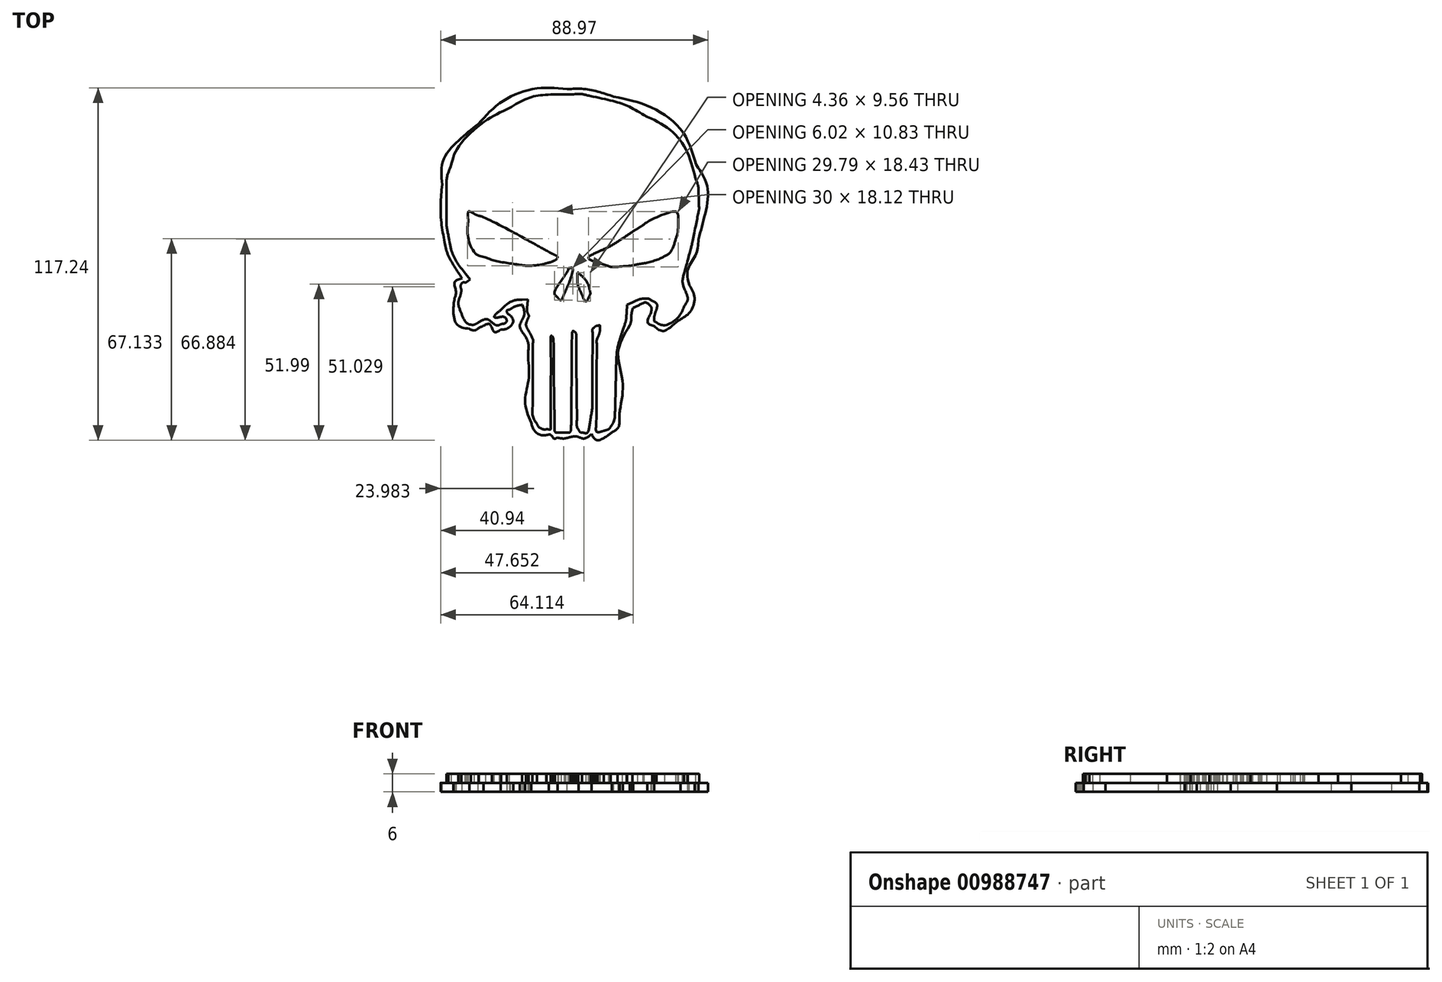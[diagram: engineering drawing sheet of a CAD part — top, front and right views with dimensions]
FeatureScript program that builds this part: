
annotation { "Feature Type Name" : "Feature", "Feature Type Description" : "" }
export const myFeature = defineFeature(function(context is Context, id is Id, definition is map)
    precondition{}
    {
        {
            var Q0;
            Q0=qCreatedBy(makeId("Top.planeOp"),FACE);
            var sketch = newSketch(context, id + "F0", { "sketchPlane" : qUnion([Q0])});
            skLineSegment(sketch, "E0", {"start": v(-15.1, -13.85) * mm, "end": v(-14.93, -11.9) * mm});
            skLineSegment(sketch, "E1", {"start": v(-14.93, -11.9) * mm, "end": v(-16.83, -12.05) * mm});
            skLineSegment(sketch, "E2", {"start": v(-34.82, -5.82) * mm, "end": v(-34.16, -5.31) * mm});
            skLineSegment(sketch, "E3", {"start": v(-34.16, -5.31) * mm, "end": v(-35.58, -3.44) * mm});
            skLineSegment(sketch, "E4", {"start": v(19.8, -12.99) * mm, "end": v(18.07, -13.76) * mm});
            skLineSegment(sketch, "E5", {"start": v(18.07, -13.76) * mm, "end": v(17.92, -16.33) * mm});
            skFitSpline(sketch, "E6", {"points": [v(-5.85, -56) * mm, v(-5.95, -55.85) * mm, v(-6.1, -50.74) * mm, v(-6.17, -44.65) * mm]});
            skFitSpline(sketch, "E7", {"points": [v(-6.17, -44.65) * mm, v(-6.3, -32.8) * mm, v(-6.66, -24.47) * mm, v(-7.03, -24.1) * mm]});
            skFitSpline(sketch, "E8", {"points": [v(-7.03, -24.1) * mm, v(-7.16, -23.97) * mm, v(-7.26, -30.62) * mm, v(-7.27, -38.88) * mm]});
            skFitSpline(sketch, "E9", {"points": [v(-7.27, -38.88) * mm, v(-7.27, -55.07) * mm, v(-7.28, -55.17) * mm, v(-8.71, -55.17) * mm]});
            skFitSpline(sketch, "E10", {"points": [v(-8.71, -55.17) * mm, v(-9.86, -55.17) * mm, v(-11.3, -54.34) * mm, v(-11.92, -53.32) * mm]});
            skFitSpline(sketch, "E11", {"points": [v(-11.92, -53.32) * mm, v(-13.14, -51.36) * mm, v(-13.36, -48.77) * mm, v(-13.28, -37.24) * mm]});
            skFitSpline(sketch, "E12", {"points": [v(-13.28, -37.24) * mm, v(-13.2, -25.74) * mm, v(-13.26, -25.16) * mm, v(-14.73, -22.3) * mm]});
            skFitSpline(sketch, "E13", {"points": [v(-14.73, -22.3) * mm, v(-15.4, -21) * mm, v(-15.46, -19.77) * mm, v(-14.92, -18.44) * mm]});
            skFitSpline(sketch, "E14", {"points": [v(-14.92, -18.44) * mm, v(-14.6, -17.66) * mm, v(-14.6, -17.34) * mm, v(-14.9, -16.64) * mm]});
            skFitSpline(sketch, "E15", {"points": [v(-14.9, -16.64) * mm, v(-15.13, -16.08) * mm, v(-15.2, -15.14) * mm, v(-15.1, -13.85) * mm]});
            skFitSpline(sketch, "E16", {"points": [v(-16.83, -12.05) * mm, v(-19.3, -12.25) * mm, v(-21.71, -13.44) * mm, v(-24.06, -15.6) * mm]});
            skFitSpline(sketch, "E17", {"points": [v(-24.06, -15.6) * mm, v(-25.97, -17.35) * mm, v(-26.08, -17.91) * mm, v(-24.52, -17.91) * mm]});
            skFitSpline(sketch, "E18", {"points": [v(-24.52, -17.91) * mm, v(-22.55, -17.91) * mm, v(-22.04, -19.45) * mm, v(-23.78, -20.17) * mm]});
            skFitSpline(sketch, "E19", {"points": [v(-23.78, -20.17) * mm, v(-24.74, -20.57) * mm, v(-25.8, -20.37) * mm, v(-26.93, -19.57) * mm]});
            skFitSpline(sketch, "E20", {"points": [v(-26.93, -19.57) * mm, v(-28.3, -18.59) * mm, v(-29.38, -18.6) * mm, v(-31.32, -19.61) * mm]});
            skFitSpline(sketch, "E21", {"points": [v(-31.32, -19.61) * mm, v(-32.62, -20.3) * mm, v(-33.25, -20.47) * mm, v(-33.82, -20.33) * mm]});
            skFitSpline(sketch, "E22", {"points": [v(-33.82, -20.33) * mm, v(-34.92, -20.05) * mm, v(-36.3, -18.42) * mm, v(-37.02, -16.56) * mm]});
            skFitSpline(sketch, "E23", {"points": [v(-37.02, -16.56) * mm, v(-37.91, -14.22) * mm, v(-38.02, -12.89) * mm, v(-37.47, -10.98) * mm]});
            skFitSpline(sketch, "E24", {"points": [v(-37.47, -10.98) * mm, v(-37.2, -10.06) * mm, v(-37.05, -8.9) * mm, v(-37.14, -8.38) * mm]});
            skFitSpline(sketch, "E25", {"points": [v(-37.14, -8.38) * mm, v(-37.3, -7.41) * mm, v(-36.62, -6.35) * mm, v(-35.84, -6.33) * mm]});
            skFitSpline(sketch, "E26", {"points": [v(-35.84, -6.33) * mm, v(-35.64, -6.33) * mm, v(-35.19, -6.1) * mm, v(-34.82, -5.82) * mm]});
            skFitSpline(sketch, "E27", {"points": [v(-35.58, -3.44) * mm, v(-38.7, 0.67) * mm, v(-40.31, 4.22) * mm, v(-41.31, 9.1) * mm]});
            skFitSpline(sketch, "E28", {"points": [v(-41.31, 9.1) * mm, v(-41.85, 11.75) * mm, v(-41.94, 13.08) * mm, v(-41.96, 19.34) * mm]});
            skFitSpline(sketch, "E29", {"points": [v(-41.96, 19.34) * mm, v(-41.98, 26.96) * mm, v(-41.71, 29.24) * mm, v(-40.4, 32.73) * mm]});
            skFitSpline(sketch, "E30", {"points": [v(-40.4, 32.73) * mm, v(-38.28, 38.4) * mm, v(-29.23, 47.3) * mm, v(-21.14, 51.66) * mm]});
            skFitSpline(sketch, "E31", {"points": [v(-21.14, 51.66) * mm, v(-15.26, 54.83) * mm, v(-10.37, 56.02) * mm, v(-2.4, 56.23) * mm]});
            skFitSpline(sketch, "E32", {"points": [v(-2.4, 56.23) * mm, v(2.5, 56.37) * mm, v(3.29, 56.32) * mm, v(5.78, 55.75) * mm]});
            skFitSpline(sketch, "E33", {"points": [v(5.78, 55.75) * mm, v(14.08, 53.86) * mm, v(18.54, 52.28) * mm, v(23.7, 49.37) * mm]});
            skFitSpline(sketch, "E34", {"points": [v(23.7, 49.37) * mm, v(32.2, 44.6) * mm, v(37.67, 37.9) * mm, v(40.88, 28.37) * mm]});
            skFitSpline(sketch, "E35", {"points": [v(40.88, 28.37) * mm, v(41.66, 26.03) * mm, v(41.8, 25.2) * mm, v(41.9, 21.88) * mm]});
            skFitSpline(sketch, "E36", {"points": [v(41.9, 21.88) * mm, v(42.03, 18.26) * mm, v(41.98, 17.8) * mm, v(40.88, 12.43) * mm]});
            skFitSpline(sketch, "E37", {"points": [v(40.88, 12.43) * mm, v(39.69, 6.62) * mm, v(39.27, 4.88) * mm, v(37.77, -0.7) * mm]});
            skFitSpline(sketch, "E38", {"points": [v(37.77, -0.7) * mm, v(36.68, -4.73) * mm, v(36.6, -6.74) * mm, v(37.47, -9.1) * mm]});
            skFitSpline(sketch, "E39", {"points": [v(37.47, -9.1) * mm, v(38.22, -11.17) * mm, v(38.12, -12.38) * mm, v(37.02, -14.35) * mm]});
            skFitSpline(sketch, "E40", {"points": [v(37.02, -14.35) * mm, v(35, -17.97) * mm, v(30.4, -20.56) * mm, v(27.8, -19.54) * mm]});
            skFitSpline(sketch, "E41", {"points": [v(27.8, -19.54) * mm, v(27.2, -19.3) * mm, v(27.14, -17.7) * mm, v(27.65, -15.8) * mm]});
            skFitSpline(sketch, "E42", {"points": [v(27.65, -15.8) * mm, v(28.1, -14.14) * mm, v(27.74, -13.13) * mm, v(26.46, -12.46) * mm]});
            skFitSpline(sketch, "E43", {"points": [v(26.46, -12.46) * mm, v(25.06, -11.73) * mm, v(22.1, -11.97) * mm, v(19.8, -12.99) * mm]});
            skFitSpline(sketch, "E44", {"points": [v(17.92, -16.33) * mm, v(17.8, -18.35) * mm, v(17.5, -19.74) * mm, v(16.47, -22.82) * mm]});
            skFitSpline(sketch, "E45", {"points": [v(16.47, -22.82) * mm, v(15.76, -24.97) * mm, v(15.03, -27.51) * mm, v(14.86, -28.46) * mm]});
            skFitSpline(sketch, "E46", {"points": [v(14.86, -28.46) * mm, v(14.7, -29.41) * mm, v(14.45, -34.32) * mm, v(14.33, -39.36) * mm]});
            skFitSpline(sketch, "E47", {"points": [v(14.33, -39.36) * mm, v(14.1, -49.03) * mm, v(13.7, -52.5) * mm, v(12.62, -54.27) * mm]});
            skFitSpline(sketch, "E48", {"points": [v(12.62, -54.27) * mm, v(12.21, -54.94) * mm, v(11.7, -55.26) * mm, v(10.32, -55.68) * mm]});
            skFitSpline(sketch, "E49", {"points": [v(10.32, -55.68) * mm, v(9.35, -55.98) * mm, v(8.38, -56.16) * mm, v(8.17, -56.08) * mm]});
            skFitSpline(sketch, "E50", {"points": [v(8.17, -56.08) * mm, v(7.86, -55.96) * mm, v(7.81, -53.23) * mm, v(7.9, -40.66) * mm]});
            skFitSpline(sketch, "E51", {"points": [v(7.9, -40.66) * mm, v(7.99, -26.57) * mm, v(8.04, -25.3) * mm, v(8.52, -24.12) * mm]});
            skFitSpline(sketch, "E52", {"points": [v(8.52, -24.12) * mm, v(8.8, -23.42) * mm, v(9.06, -22.34) * mm, v(9.08, -21.72) * mm]});
            skFitSpline(sketch, "E53", {"points": [v(9.08, -21.72) * mm, v(9.1, -20.68) * mm, v(9.05, -20.6) * mm, v(8.4, -20.67) * mm]});
            skFitSpline(sketch, "E54", {"points": [v(8.4, -20.67) * mm, v(8.01, -20.72) * mm, v(7.44, -21) * mm, v(7.13, -21.32) * mm]});
            skFitSpline(sketch, "E55", {"points": [v(7.13, -21.32) * mm, v(6.58, -21.86) * mm, v(6.57, -22.26) * mm, v(6.55, -34.92) * mm]});
            skFitSpline(sketch, "E56", {"points": [v(6.55, -34.92) * mm, v(6.54, -45.74) * mm, v(6.46, -48.46) * mm, v(6.07, -50.85) * mm]});
            skFitSpline(sketch, "E57", {"points": [v(6.07, -50.85) * mm, v(5.36, -55.2) * mm, v(4.69, -56.43) * mm, v(3.15, -56.24) * mm]});
            skFitSpline(sketch, "E58", {"points": [v(3.15, -56.24) * mm, v(2.6, -56.18) * mm, v(2.24, -55.87) * mm, v(1.89, -55.17) * mm]});
            skFitSpline(sketch, "E59", {"points": [v(1.89, -55.17) * mm, v(1.44, -54.27) * mm, v(1.38, -52.77) * mm, v(1.27, -38.71) * mm]});
            skFitSpline(sketch, "E60", {"points": [v(1.27, -38.71) * mm, v(1.17, -24.85) * mm, v(1.1, -23.2) * mm, v(0.7, -22.78) * mm]});
            skFitSpline(sketch, "E61", {"points": [v(0.7, -22.78) * mm, v(0.44, -22.53) * mm, v(0.13, -22.42) * mm, v(0.02, -22.53) * mm]});
            skFitSpline(sketch, "E62", {"points": [v(0.02, -22.53) * mm, v(-0.1, -22.65) * mm, v(-0.27, -30.07) * mm, v(-0.37, -39.03) * mm]});
            skFitSpline(sketch, "E63", {"points": [v(-0.37, -39.03) * mm, v(-0.47, -47.98) * mm, v(-0.64, -55.53) * mm, v(-0.76, -55.8) * mm]});
            skFitSpline(sketch, "E64", {"points": [v(-0.76, -55.8) * mm, v(-0.94, -56.21) * mm, v(-1.35, -56.3) * mm, v(-3.32, -56.3) * mm]});
            skFitSpline(sketch, "E65", {"points": [v(-3.32, -56.3) * mm, v(-4.62, -56.3) * mm, v(-5.76, -56.17) * mm, v(-5.85, -56) * mm]});
            skFitSpline(sketch, "E66", {"points": [v(5.34, -11.25) * mm, v(5.84, -10.11) * mm, v(5.87, -9.8) * mm, v(5.59, -8.64) * mm]});
            skFitSpline(sketch, "E67", {"points": [v(5.59, -8.64) * mm, v(5.21, -7.15) * mm, v(4.02, -5.15) * mm, v(2.8, -3.98) * mm]});
            skFitSpline(sketch, "E68", {"points": [v(2.8, -3.98) * mm, v(1.78, -3.01) * mm, v(1.58, -3.26) * mm, v(1.6, -5.46) * mm]});
            skFitSpline(sketch, "E69", {"points": [v(1.6, -5.46) * mm, v(1.6, -6.77) * mm, v(1.84, -7.65) * mm, v(2.8, -9.82) * mm]});
            skFitSpline(sketch, "E70", {"points": [v(2.8, -9.82) * mm, v(3.48, -11.32) * mm, v(4.19, -12.55) * mm, v(4.4, -12.55) * mm]});
            skFitSpline(sketch, "E71", {"points": [v(4.4, -12.55) * mm, v(4.6, -12.55) * mm, v(5.02, -11.97) * mm, v(5.34, -11.25) * mm]});
            skFitSpline(sketch, "E72", {"points": [v(-2.81, -10.13) * mm, v(-0.96, -5.72) * mm, v(-0.1, -1.54) * mm, v(-1.05, -1.54) * mm]});
            skFitSpline(sketch, "E73", {"points": [v(-1.05, -1.54) * mm, v(-1.29, -1.54) * mm, v(-1.48, -1.71) * mm, v(-1.48, -1.91) * mm]});
            skFitSpline(sketch, "E74", {"points": [v(-1.48, -1.91) * mm, v(-1.48, -2.12) * mm, v(-2.04, -3.13) * mm, v(-2.73, -4.15) * mm]});
            skFitSpline(sketch, "E75", {"points": [v(-2.73, -4.15) * mm, v(-5.52, -8.31) * mm, v(-6.01, -10.04) * mm, v(-4.83, -11.54) * mm]});
            skFitSpline(sketch, "E76", {"points": [v(-4.83, -11.54) * mm, v(-4.5, -11.95) * mm, v(-4.1, -12.25) * mm, v(-3.94, -12.2) * mm]});
            skFitSpline(sketch, "E77", {"points": [v(-3.94, -12.2) * mm, v(-3.77, -12.14) * mm, v(-3.26, -11.21) * mm, v(-2.81, -10.13) * mm]});
            skFitSpline(sketch, "E78", {"points": [v(21.52, -0.3) * mm, v(24.61, 0.26) * mm, v(29.02, 1.61) * mm, v(30.56, 2.48) * mm]});
            skFitSpline(sketch, "E79", {"points": [v(30.56, 2.48) * mm, v(32.04, 3.33) * mm, v(33.34, 5.3) * mm, v(34.26, 8.15) * mm]});
            skFitSpline(sketch, "E80", {"points": [v(34.26, 8.15) * mm, v(34.87, 10.01) * mm, v(35.02, 11.03) * mm, v(35.04, 13.46) * mm]});
            skFitSpline(sketch, "E81", {"points": [v(35.04, 13.46) * mm, v(35.06, 15.12) * mm, v(34.97, 16.57) * mm, v(34.85, 16.7) * mm]});
            skFitSpline(sketch, "E82", {"points": [v(34.85, 16.7) * mm, v(34.22, 17.32) * mm, v(26.09, 14.53) * mm, v(23.38, 12.76) * mm]});
            skFitSpline(sketch, "E83", {"points": [v(23.38, 12.76) * mm, v(22.82, 12.4) * mm, v(21.86, 11.78) * mm, v(21.24, 11.4) * mm]});
            skFitSpline(sketch, "E84", {"points": [v(21.24, 11.4) * mm, v(20.62, 11.01) * mm, v(18.45, 9.59) * mm, v(16.4, 8.24) * mm]});
            skFitSpline(sketch, "E85", {"points": [v(16.4, 8.24) * mm, v(14.37, 6.88) * mm, v(11.6, 5.29) * mm, v(10.27, 4.7) * mm]});
            skFitSpline(sketch, "E86", {"points": [v(10.27, 4.7) * mm, v(7.78, 3.6) * mm, v(5.3, 2.16) * mm, v(5.3, 1.83) * mm]});
            skFitSpline(sketch, "E87", {"points": [v(5.3, 1.83) * mm, v(5.3, 1.57) * mm, v(8.19, 0.3) * mm, v(10.1, -0.28) * mm]});
            skFitSpline(sketch, "E88", {"points": [v(10.1, -0.28) * mm, v(10.95, -0.54) * mm, v(11.77, -0.8) * mm, v(11.93, -0.86) * mm]});
            skFitSpline(sketch, "E89", {"points": [v(11.93, -0.86) * mm, v(12.56, -1.1) * mm, v(19.16, -0.72) * mm, v(21.52, -0.3) * mm]});
            skFitSpline(sketch, "E90", {"points": [v(-9.09, 0.01) * mm, v(-7.34, 0.47) * mm, v(-5.44, 1.38) * mm, v(-5.09, 1.95) * mm]});
            skFitSpline(sketch, "E91", {"points": [v(-5.09, 1.95) * mm, v(-4.96, 2.15) * mm, v(-5.39, 2.52) * mm, v(-6.21, 2.94) * mm]});
            skFitSpline(sketch, "E92", {"points": [v(-6.21, 2.94) * mm, v(-6.95, 3.31) * mm, v(-10.34, 5.17) * mm, v(-13.75, 7.06) * mm]});
            skFitSpline(sketch, "E93", {"points": [v(-13.75, 7.06) * mm, v(-19.78, 10.4) * mm, v(-29.68, 15.4) * mm, v(-31.11, 15.82) * mm]});
            skFitSpline(sketch, "E94", {"points": [v(-31.11, 15.82) * mm, v(-31.5, 15.93) * mm, v(-32.3, 16.27) * mm, v(-32.9, 16.57) * mm]});
            skFitSpline(sketch, "E95", {"points": [v(-32.9, 16.57) * mm, v(-34.5, 17.38) * mm, v(-34.78, 17) * mm, v(-34.78, 14) * mm]});
            skFitSpline(sketch, "E96", {"points": [v(-34.78, 14) * mm, v(-34.78, 8.58) * mm, v(-32.21, 3.2) * mm, v(-29.07, 2.04) * mm]});
            skFitSpline(sketch, "E97", {"points": [v(-29.07, 2.04) * mm, v(-26.73, 1.18) * mm, v(-21.98, 0.18) * mm, v(-16.86, -0.53) * mm]});
            skFitSpline(sketch, "E98", {"points": [v(-16.86, -0.53) * mm, v(-15.3, -0.75) * mm, v(-10.8, -0.43) * mm, v(-9.09, 0.01) * mm]});
            skSolve(sketch);
        }
        {
            var Q0;
            Q0=makeQuery(id+"F0.imprint","IMPRINT",FACE,{"disambiguationData":[TD([[makeQuery(id+"F0.imprint","IMPRINT",EDGE,{"derivedFrom":sQuery(id+"F0.wireOp",EDGE,"E0")}),-1.0]])]});
            extrude(context, id + "F1", {"entities" : qUnion([Q0]), "depth" : 3 * mm, "offsetDistance" : 25 * mm});
        }
        {
            var Q0;
            Q0=qCreatedBy(makeId("Top.planeOp"),FACE);
            var sketch = newSketch(context, id + "F2", { "sketchPlane" : qUnion([Q0])});
            skFitSpline(sketch, "E99", {"points": [v(-1.87, 58.02) * mm, v(-12.82, 58.11) * mm, v(-23.63, 53.77) * mm, v(-31.5, 46.33) * mm]});
            skFitSpline(sketch, "E100", {"points": [v(-31.5, 46.33) * mm, v(-37.54, 41.31) * mm, v(-43.02, 34.42) * mm, v(-43.4, 26.23) * mm]});
            skFitSpline(sketch, "E101", {"points": [v(-43.4, 26.23) * mm, v(-43.92, 19.83) * mm, v(-43.65, 13.36) * mm, v(-42.56, 7.04) * mm]});
            skFitSpline(sketch, "E102", {"points": [v(-42.56, 7.04) * mm, v(-41.43, 2.72) * mm, v(-39.2, -1.21) * mm, v(-36.8, -4.94) * mm]});
            skFitSpline(sketch, "E103", {"points": [v(-36.8, -4.94) * mm, v(-39.3, -6.26) * mm, v(-38.84, -9.26) * mm, v(-39.28, -11.6) * mm]});
            skFitSpline(sketch, "E104", {"points": [v(-39.28, -11.6) * mm, v(-39.7, -15.44) * mm, v(-38.44, -20.34) * mm, v(-34.4, -21.72) * mm]});
            skFitSpline(sketch, "E105", {"points": [v(-34.4, -21.72) * mm, v(-32.71, -22.29) * mm, v(-31.09, -21.42) * mm, v(-29.63, -20.7) * mm]});
            skFitSpline(sketch, "E106", {"points": [v(-29.63, -20.7) * mm, v(-27.56, -20.26) * mm, v(-26.1, -22.77) * mm, v(-23.99, -21.99) * mm]});
            skFitSpline(sketch, "E107", {"points": [v(-23.99, -21.99) * mm, v(-21.91, -21.66) * mm, v(-19.8, -19.47) * mm, v(-20.67, -17.27) * mm]});
            skFitSpline(sketch, "E108", {"points": [v(-20.67, -17.27) * mm, v(-21.37, -16.88) * mm, v(-21.96, -15.7) * mm, v(-20.94, -15.32) * mm]});
            skFitSpline(sketch, "E109", {"points": [v(-20.94, -15.32) * mm, v(-19.67, -14.52) * mm, v(-18.23, -14.02) * mm, v(-16.77, -13.73) * mm]});
            skFitSpline(sketch, "E110", {"points": [v(-16.77, -13.73) * mm, v(-16.12, -17.14) * mm, v(-17.55, -20.72) * mm, v(-15.9, -23.95) * mm]});
            skFitSpline(sketch, "E111", {"points": [v(-15.9, -23.95) * mm, v(-14.85, -26.25) * mm, v(-14.74, -28.77) * mm, v(-14.86, -31.25) * mm]});
            skFitSpline(sketch, "E112", {"points": [v(-14.86, -31.25) * mm, v(-14.65, -38.49) * mm, v(-15.85, -45.95) * mm, v(-13.8, -53.02) * mm]});
            skFitSpline(sketch, "E113", {"points": [v(-13.8, -53.02) * mm, v(-12.91, -55.4) * mm, v(-10.53, -57.12) * mm, v(-7.97, -56.88) * mm]});
            skFitSpline(sketch, "E114", {"points": [v(-7.97, -56.88) * mm, v(-6.98, -57.26) * mm, v(-6.26, -58.27) * mm, v(-5.08, -57.95) * mm]});
            skFitSpline(sketch, "E115", {"points": [v(-5.08, -57.95) * mm, v(-2.77, -58.22) * mm, v(-0.31, -57.65) * mm, v(1.94, -57.63) * mm]});
            skFitSpline(sketch, "E116", {"points": [v(1.94, -57.63) * mm, v(3.4, -58.24) * mm, v(5.1, -57.73) * mm, v(6.23, -56.69) * mm]});
            skFitSpline(sketch, "E117", {"points": [v(6.23, -56.69) * mm, v(7.96, -58.78) * mm, v(11.15, -57.61) * mm, v(12.96, -56.24) * mm]});
            skFitSpline(sketch, "E118", {"points": [v(12.96, -56.24) * mm, v(15.19, -54.5) * mm, v(15.57, -51.58) * mm, v(15.62, -48.96) * mm]});
            skFitSpline(sketch, "E119", {"points": [v(15.62, -48.96) * mm, v(16.58, -39.51) * mm, v(15.12, -29.53) * mm, v(19, -20.56) * mm]});
            skFitSpline(sketch, "E120", {"points": [v(19, -20.56) * mm, v(19.5, -18.66) * mm, v(19.56, -16.67) * mm, v(20.07, -14.77) * mm]});
            skFitSpline(sketch, "E121", {"points": [v(20.07, -14.77) * mm, v(21.91, -13.93) * mm, v(24.35, -13.01) * mm, v(26.14, -14.48) * mm]});
            skFitSpline(sketch, "E122", {"points": [v(26.14, -14.48) * mm, v(25.96, -16.56) * mm, v(24.9, -19.5) * mm, v(27.12, -20.85) * mm]});
            skFitSpline(sketch, "E123", {"points": [v(27.12, -20.85) * mm, v(30.14, -22.47) * mm, v(33.52, -20.33) * mm, v(35.92, -18.55) * mm]});
            skFitSpline(sketch, "E124", {"points": [v(35.92, -18.55) * mm, v(39.17, -15.92) * mm, v(40.5, -11.15) * mm, v(38.8, -7.3) * mm]});
            skFitSpline(sketch, "E125", {"points": [v(38.8, -7.3) * mm, v(38.3, -1.98) * mm, v(40.91, 2.9) * mm, v(41.81, 8.02) * mm]});
            skFitSpline(sketch, "E126", {"points": [v(41.81, 8.02) * mm, v(43.93, 16.1) * mm, v(44.85, 25.13) * mm, v(41.08, 32.9) * mm]});
            skFitSpline(sketch, "E127", {"points": [v(41.08, 32.9) * mm, v(36.16, 44.29) * mm, v(25.4, 52.23) * mm, v(13.64, 55.5) * mm]});
            skFitSpline(sketch, "E128", {"points": [v(13.64, 55.5) * mm, v(8.63, 57.1) * mm, v(3.36, 58.1) * mm, v(-1.87, 58.02) * mm]});
            skSolve(sketch);
        }
        {
            var Q0;
            Q0 = qSketchRegion(id + "F2", true);
            extrude(context, id + "F3", {"entities" : qUnion([Q0]), "oppositeDirection" : true, "depth" : 3 * mm, "offsetDistance" : 25 * mm});
        }
    });
